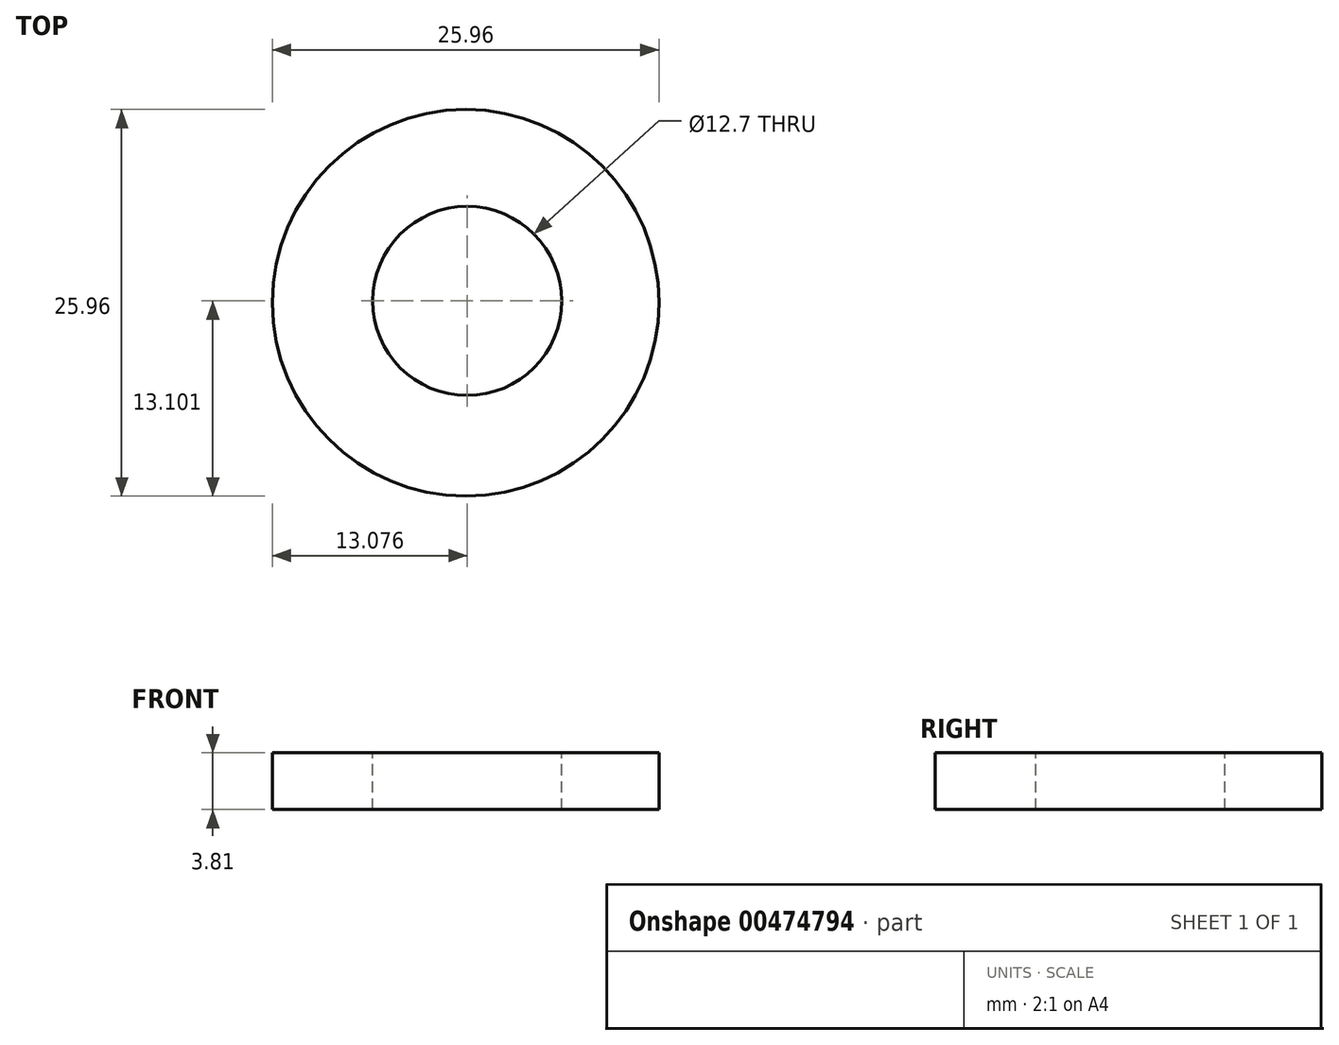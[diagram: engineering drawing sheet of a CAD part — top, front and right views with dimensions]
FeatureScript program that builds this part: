
annotation { "Feature Type Name" : "Feature", "Feature Type Description" : "" }
export const myFeature = defineFeature(function(context is Context, id is Id, definition is map)
    precondition{}
    {
        {
            var Q0;
            Q0=qCreatedBy(makeId("Top.planeOp"),FACE);
            var sketch = newSketch(context, id + "F0", { "sketchPlane" : qUnion([Q0])});
            skCircle(sketch, "E0", {"center": v(0, 0) * mm, "radius": 12.98 * mm});
            skSolve(sketch);
        }
        {
            var Q0;
            Q0=makeQuery(id+"F0.imprint","IMPRINT",FACE,{"disambiguationData":[TD([[makeQuery(id+"F0.imprint","IMPRINT",EDGE,{"derivedFrom":sQuery(id+"F0.wireOp",EDGE,"E0")}),1.0]])]});
            extrude(context, id + "F1", {"entities" : qUnion([Q0]), "oppositeDirection" : true, "depth" : 3.8 * mm});
        }
        {
            var Q0;
            Q0=makeQuery(id+"F1.opExtrude","CAP_FACE",FACE,{"disambiguationData":[OSD([sQuery(id+"F0.wireOp",EDGE,"E0")])],"isStart":true});
            var sketch = newSketch(context, id + "F2", { "sketchPlane" : qUnion([Q0])});
            skPoint(sketch, "E1", {"position": v(0, 0) * mm});
            skPoint(sketch, "E2", {"position": v(0.1, 0.12) * mm});
            skCircle(sketch, "E3", {"center": v(0.1, 0.12) * mm, "radius": 6.41 * mm});
            skSolve(sketch);
        }
        {
            var Q0;
            Q0=sQuery(id+"F2.wireOp",VERTEX,"E2");
            var Q1;
            Q1=makeQuery(id+"F1.opExtrude","SWEPT_BODY",BODY,{"disambiguationData":[OSD([sQuery(id+"F0.wireOp",EDGE,"E0")])]});
            hole(context, id + "F3", {"style" : HoleStyle.SIMPLE, "endStyle" : HoleEndStyle.BLIND, "holeDiameter" : 12.7 * mm, "holeDepth" : 12.7 * mm, "isTappedThrough" : true, "tappedDepth" : 12.7 * mm, "tapClearance" : 3, "locations" : qUnion([Q0]), "scope" : qUnion([Q1])});
        }
    });
